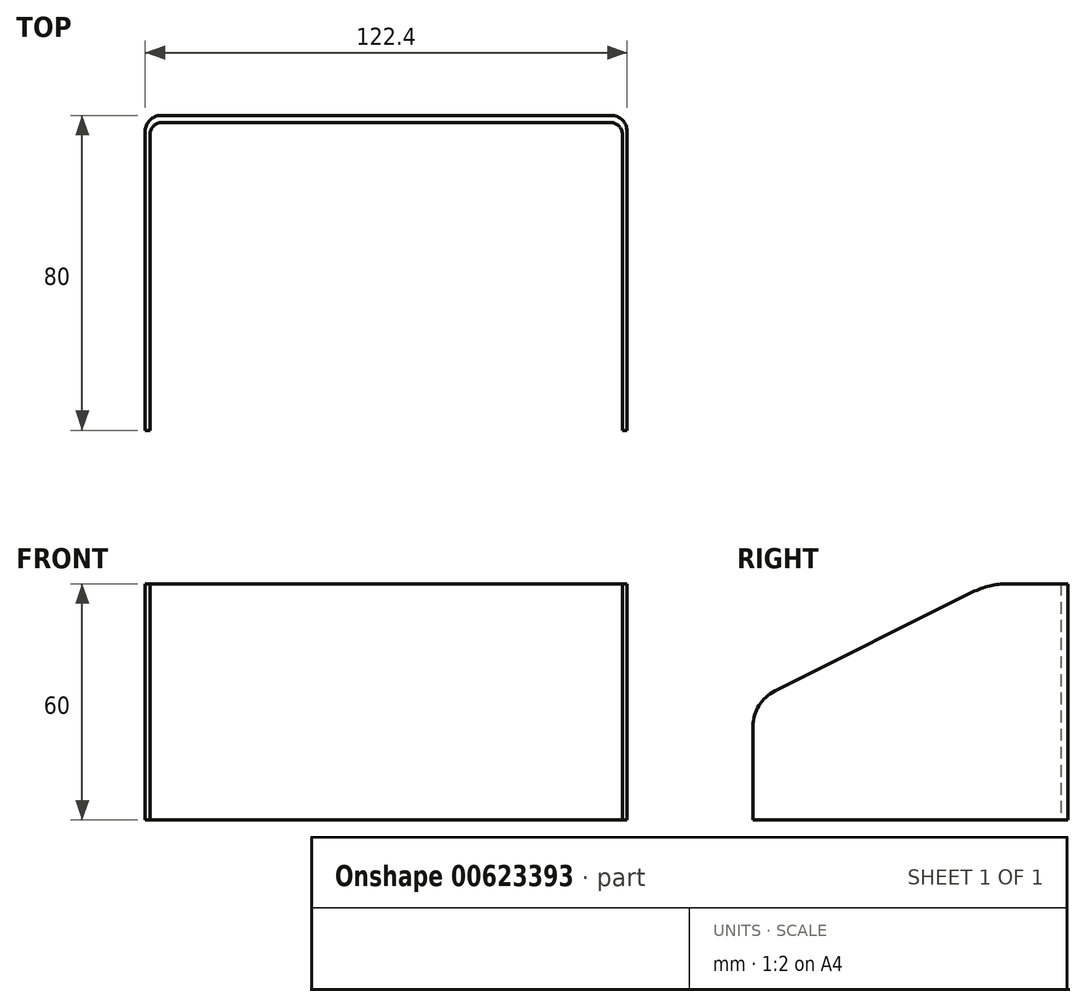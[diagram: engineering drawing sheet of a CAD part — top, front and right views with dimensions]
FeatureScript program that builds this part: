
annotation { "Feature Type Name" : "Feature", "Feature Type Description" : "" }
export const myFeature = defineFeature(function(context is Context, id is Id, definition is map)
    precondition{}
    {
        {
            var Q0;
            Q0=qCreatedBy(makeId("Top.planeOp"),FACE);
            var sketch = newSketch(context, id + "F0", { "sketchPlane" : qUnion([Q0])});
            skLineSegment(sketch, "E0", {"start": v(-69.05, -43.25) * mm, "end": v(-67.85, -43.25) * mm});
            skLineSegment(sketch, "E1", {"start": v(-67.85, -43.25) * mm, "end": v(-67.85, 34.95) * mm});
            skLineSegment(sketch, "E2", {"start": v(-67.85, 34.95) * mm, "end": v(52.15, 34.95) * mm});
            skLineSegment(sketch, "E3", {"start": v(52.15, 34.95) * mm, "end": v(52.15, -43.25) * mm});
            skLineSegment(sketch, "E4", {"start": v(52.15, -43.25) * mm, "end": v(53.35, -43.25) * mm});
            skLineSegment(sketch, "E5", {"start": v(53.35, -43.25) * mm, "end": v(53.35, 36.75) * mm});
            skLineSegment(sketch, "E6", {"start": v(53.35, 36.75) * mm, "end": v(-69.05, 36.75) * mm});
            skLineSegment(sketch, "E7", {"start": v(-69.05, 36.75) * mm, "end": v(-69.05, -43.25) * mm});
            skSolve(sketch);
        }
        {
            var Q0;
            Q0=makeQuery(id+"F0.imprint","IMPRINT",FACE,{"disambiguationData":[TD([[makeQuery(id+"F0.imprint","IMPRINT",EDGE,{"derivedFrom":sQuery(id+"F0.wireOp",EDGE,"E0")}),1.0]])]});
            extrude(context, id + "F1", {"entities" : qUnion([Q0]), "depth" : 60 * mm, "offsetDistance" : 25 * mm});
        }
        {
            var Q0;
            Q0=makeQuery(id+"F1.opExtrude","CAP_EDGE",EDGE,{"disambiguationData":[OSD([sQuery(id+"F0.wireOp",EDGE,"E0")])],"isStart":false});
            var Q1;
            Q1=makeQuery(id+"F1.opExtrude","CAP_EDGE",EDGE,{"disambiguationData":[OSD([sQuery(id+"F0.wireOp",EDGE,"E4")])],"isStart":false});
            chamfer(context, id + "F2", {"entities" : qUnion([Q0, Q1]), "chamferType" : ChamferType.TWO_OFFSETS, "width1" : 60 * mm, "oppositeDirection" : false, "width2" : 30 * mm, "tangentPropagation" : true});
        }
        {
            var Q0;
            {var subQ0=sQuery(id+"F0.wireOp",EDGE,"E0");Q0=makeQuery(id+"F2.opChamfer","BLEND_EDGE",EDGE,{"blendedFrom":[makeQuery(id+"F1.opExtrude","CAP_EDGE",EDGE,{"disambiguationData":[OSD([subQ0])],"isStart":false}),makeQuery(id+"F1.opExtrude","CAP_FACE",FACE,{"disambiguationData":[OSD([subQ0,sQuery(id+"F0.wireOp",EDGE,"E1"),sQuery(id+"F0.wireOp",EDGE,"E2"),sQuery(id+"F0.wireOp",EDGE,"E3"),sQuery(id+"F0.wireOp",EDGE,"E4"),sQuery(id+"F0.wireOp",EDGE,"E5"),sQuery(id+"F0.wireOp",EDGE,"E6"),sQuery(id+"F0.wireOp",EDGE,"E7")])],"isStart":false})],"blendedInto":[makeQuery(id+"F1.opExtrude","CAP_FACE",FACE,{"disambiguationData":[OSD([subQ0,sQuery(id+"F0.wireOp",EDGE,"E1"),sQuery(id+"F0.wireOp",EDGE,"E2"),sQuery(id+"F0.wireOp",EDGE,"E3"),sQuery(id+"F0.wireOp",EDGE,"E4"),sQuery(id+"F0.wireOp",EDGE,"E5"),sQuery(id+"F0.wireOp",EDGE,"E6"),sQuery(id+"F0.wireOp",EDGE,"E7")])],"isStart":false})]});}
            var Q1;
            {var subQ0=sQuery(id+"F0.wireOp",EDGE,"E4");Q1=makeQuery(id+"F2.opChamfer","BLEND_EDGE",EDGE,{"blendedFrom":[makeQuery(id+"F1.opExtrude","CAP_EDGE",EDGE,{"disambiguationData":[OSD([subQ0])],"isStart":false}),makeQuery(id+"F1.opExtrude","CAP_FACE",FACE,{"disambiguationData":[OSD([sQuery(id+"F0.wireOp",EDGE,"E0"),sQuery(id+"F0.wireOp",EDGE,"E1"),sQuery(id+"F0.wireOp",EDGE,"E2"),sQuery(id+"F0.wireOp",EDGE,"E3"),subQ0,sQuery(id+"F0.wireOp",EDGE,"E5"),sQuery(id+"F0.wireOp",EDGE,"E6"),sQuery(id+"F0.wireOp",EDGE,"E7")])],"isStart":false})],"blendedInto":[makeQuery(id+"F1.opExtrude","CAP_FACE",FACE,{"disambiguationData":[OSD([sQuery(id+"F0.wireOp",EDGE,"E0"),sQuery(id+"F0.wireOp",EDGE,"E1"),sQuery(id+"F0.wireOp",EDGE,"E2"),sQuery(id+"F0.wireOp",EDGE,"E3"),subQ0,sQuery(id+"F0.wireOp",EDGE,"E5"),sQuery(id+"F0.wireOp",EDGE,"E6"),sQuery(id+"F0.wireOp",EDGE,"E7")])],"isStart":false})]});}
            fillet(context, id + "F3", {"entities" : qUnion([Q0, Q1]), "radius" : 20 * mm, "tangentPropagation" : true, "allowEdgeOverflow" : false});
        }
        {
            var Q0;
            {var subQ0=sQuery(id+"F0.wireOp",EDGE,"E0");Q0=makeQuery(id+"F2.opChamfer","BLEND_EDGE",EDGE,{"blendedFrom":[makeQuery(id+"F1.opExtrude","CAP_EDGE",EDGE,{"disambiguationData":[OSD([subQ0])],"isStart":false}),makeQuery(id+"F1.opExtrude","SWEPT_FACE",FACE,{"disambiguationData":[OSD([subQ0])]})],"blendedInto":[makeQuery(id+"F1.opExtrude","SWEPT_FACE",FACE,{"disambiguationData":[OSD([subQ0])]})]});}
            var Q1;
            {var subQ0=sQuery(id+"F0.wireOp",EDGE,"E4");Q1=makeQuery(id+"F2.opChamfer","BLEND_EDGE",EDGE,{"blendedFrom":[makeQuery(id+"F1.opExtrude","CAP_EDGE",EDGE,{"disambiguationData":[OSD([subQ0])],"isStart":false}),makeQuery(id+"F1.opExtrude","SWEPT_FACE",FACE,{"disambiguationData":[OSD([subQ0])]})],"blendedInto":[makeQuery(id+"F1.opExtrude","SWEPT_FACE",FACE,{"disambiguationData":[OSD([subQ0])]})]});}
            fillet(context, id + "F4", {"entities" : qUnion([Q0, Q1]), "radius" : 10 * mm, "tangentPropagation" : true, "allowEdgeOverflow" : false});
        }
        {
            var Q0;
            Q0=makeQuery(id+"F1.opExtrude","SWEPT_EDGE",EDGE,{"disambiguationData":[OSD([sQuery(id+"F0.wireOp",EDGE,"E1"),sQuery(id+"F0.wireOp",EDGE,"E2")])]});
            var Q1;
            Q1=makeQuery(id+"F1.opExtrude","SWEPT_EDGE",EDGE,{"disambiguationData":[OSD([sQuery(id+"F0.wireOp",EDGE,"E2"),sQuery(id+"F0.wireOp",EDGE,"E3")])]});
            fillet(context, id + "F5", {"entities" : qUnion([Q0, Q1]), "radius" : 3 * mm, "tangentPropagation" : true, "allowEdgeOverflow" : false});
        }
        {
            var Q0;
            Q0=makeQuery(id+"F1.opExtrude","SWEPT_EDGE",EDGE,{"disambiguationData":[OSD([sQuery(id+"F0.wireOp",EDGE,"E5"),sQuery(id+"F0.wireOp",EDGE,"E6")])]});
            var Q1;
            Q1=makeQuery(id+"F1.opExtrude","SWEPT_EDGE",EDGE,{"disambiguationData":[OSD([sQuery(id+"F0.wireOp",EDGE,"E6"),sQuery(id+"F0.wireOp",EDGE,"E7")])]});
            fillet(context, id + "F6", {"entities" : qUnion([Q0, Q1]), "radius" : 4 * mm, "tangentPropagation" : true, "allowEdgeOverflow" : false});
        }
    });
